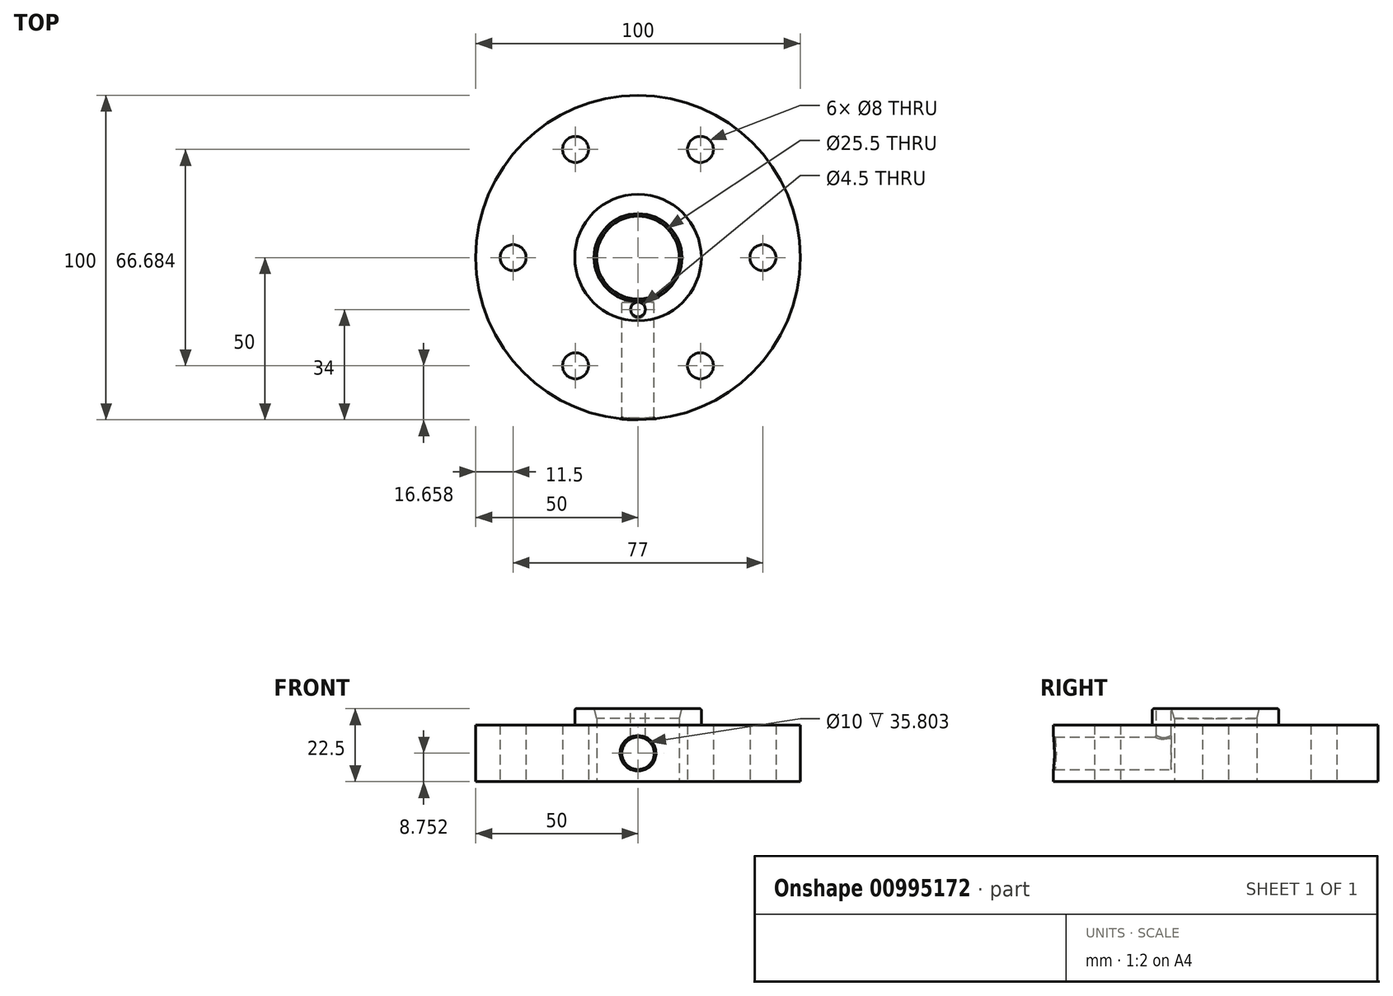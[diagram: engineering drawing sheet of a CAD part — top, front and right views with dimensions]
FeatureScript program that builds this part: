
annotation { "Feature Type Name" : "Feature", "Feature Type Description" : "" }
export const myFeature = defineFeature(function(context is Context, id is Id, definition is map)
    precondition{}
    {
        {
            var Q0;
            Q0=qCreatedBy(makeId("Top.planeOp"),FACE);
            var sketch = newSketch(context, id + "F0", { "sketchPlane" : qUnion([Q0])});
            skCircle(sketch, "E0", {"center": v(0, 0) * mm, "radius": 50 * mm});
            skCircle(sketch, "E1", {"center": v(0, 0) * mm, "radius": 19.5 * mm});
            skCircle(sketch, "E2", {"center": v(0, 0) * mm, "radius": 12.75 * mm});
            skCircle(sketch, "E3", {"center": v(-38.5, 0) * mm, "radius": 4 * mm});
            skCircle(sketch, "E4.1.0", {"center": v(-19.25, -33.34) * mm, "radius": 4 * mm});
            skCircle(sketch, "E4.2.0", {"center": v(19.25, -33.34) * mm, "radius": 4 * mm});
            skCircle(sketch, "E4.3.0", {"center": v(38.5, 0) * mm, "radius": 4 * mm});
            skCircle(sketch, "E4.4.0", {"center": v(19.25, 33.34) * mm, "radius": 4 * mm});
            skCircle(sketch, "E4.5.0", {"center": v(-19.25, 33.34) * mm, "radius": 4 * mm});
            skSolve(sketch);
        }
        {
            var Q0;
            Q0=makeQuery(id+"F0.imprint","IMPRINT",FACE,{"disambiguationData":[TD([[makeQuery(id+"F0.imprint","IMPRINT",EDGE,{"derivedFrom":sQuery(id+"F0.wireOp",EDGE,"E0")}),1.0]])]});
            extrude(context, id + "F1", {"entities" : qUnion([Q0]), "depth" : 17.5 * mm, "offsetDistance" : 25 * mm});
        }
        {
            var Q0;
            Q0=makeQuery(id+"F0.imprint","IMPRINT",FACE,{"disambiguationData":[TD([[makeQuery(id+"F0.imprint","IMPRINT",EDGE,{"derivedFrom":sQuery(id+"F0.wireOp",EDGE,"E1")}),1.0]])]});
            extrude(context, id + "F2", {"entities" : qUnion([Q0]), "operationType" : NewBodyOperationType.ADD, "depth" : 22.5 * mm, "offsetDistance" : 25 * mm});
        }
        {
            var Q0;
            Q0=qCreatedBy(makeId("Front.planeOp"),FACE);
            cPlane(context, id + "F3", {"entities" : qUnion([Q0]), "cplaneType" : CPlaneType.OFFSET, "offset" : 13.7 * mm, "width" : 150 * mm, "height" : 150 * mm});
        }
        {
            var Q0;
            Q0=qCreatedBy(id+"F3.planeOp",FACE);
            var sketch = newSketch(context, id + "F4", { "sketchPlane" : qUnion([Q0])});
            skCircle(sketch, "E5", {"center": v(0, 8.75) * mm, "radius": 5 * mm});
            skSolve(sketch);
        }
        {
            var Q0;
            Q0 = qSketchRegion(id + "F4", true);
            extrude(context, id + "F5", {"entities" : qUnion([Q0]), "operationType" : NewBodyOperationType.REMOVE, "depth" : 52 * mm, "offsetDistance" : 25 * mm});
        }
        {
            var Q0;
            Q0=makeQuery(id+"F2.opExtrude","CAP_FACE",FACE,{"disambiguationData":[OSD([sQuery(id+"F0.wireOp",EDGE,"E1"),sQuery(id+"F0.wireOp",EDGE,"E2")])],"isStart":false});
            var sketch = newSketch(context, id + "F6", { "sketchPlane" : qUnion([Q0])});
            skCircle(sketch, "E6", {"center": v(0, -16) * mm, "radius": 2.25 * mm});
            skSolve(sketch);
        }
        {
            var Q0;
            Q0=makeQuery(id+"F6.imprint","IMPRINT",FACE,{"disambiguationData":[TD([[makeQuery(id+"F6.imprint","IMPRINT",EDGE,{"derivedFrom":sQuery(id+"F6.wireOp",EDGE,"E6")}),1.0]])]});
            extrude(context, id + "F7", {"entities" : qUnion([Q0]), "operationType" : NewBodyOperationType.REMOVE, "oppositeDirection" : true, "depth" : 10 * mm, "offsetDistance" : 25 * mm});
        }
        {
            var Q0;
            Q0=makeQuery(id+"F2.opExtrude","CAP_EDGE",EDGE,{"disambiguationData":[OSD([sQuery(id+"F0.wireOp",EDGE,"E2")])],"isStart":false});
            chamfer(context, id + "F8", {"entities" : qUnion([Q0]), "chamferType" : ChamferType.OFFSET_ANGLE, "width" : 3 * mm, "oppositeDirection" : false, "angle" : 15 * degree, "tangentPropagation" : true});
        }
        {
            var Q0;
            Q0=makeQuery(id+"F2.opExtrude","CAP_EDGE",EDGE,{"disambiguationData":[OSD([sQuery(id+"F0.wireOp",EDGE,"E1")])],"isStart":false});
            var Q1;
            Q1=makeQuery(id+"F7.boolean.opBoolean","COPY",EDGE,{"derivedFrom":makeQuery(id+"F7.opExtrude","CAP_EDGE",EDGE,{"disambiguationData":[OSD([sQuery(id+"F6.wireOp",EDGE,"E6")])],"isStart":true})});
            var Q2;
            Q2=makeQuery(id+"F5.boolean.opBoolean","INTERSECT",EDGE,{"derivedFrom":[makeQuery(id+"F1.opExtrude","SWEPT_FACE",FACE,{"disambiguationData":[OSD([sQuery(id+"F0.wireOp",EDGE,"E0")])]}),makeQuery(id+"F5.opExtrude","SWEPT_FACE",FACE,{"disambiguationData":[OSD([sQuery(id+"F4.wireOp",EDGE,"E5")])]})]});
            fillet(context, id + "F9", {"entities" : qUnion([Q0, Q1, Q2]), "radius" : .5 * mm, "tangentPropagation" : true, "allowEdgeOverflow" : false});
        }
        {
            var Q0;
            Q0=makeQuery(id+"F7.boolean.opBoolean","INTERSECT",EDGE,{"derivedFrom":[makeQuery(id+"F5.boolean.opBoolean","COPY",FACE,{"derivedFrom":makeQuery(id+"F5.opExtrude","SWEPT_FACE",FACE,{"disambiguationData":[OSD([sQuery(id+"F4.wireOp",EDGE,"E5")])]})}),makeQuery(id+"F7.opExtrude","SWEPT_FACE",FACE,{"disambiguationData":[OSD([sQuery(id+"F6.wireOp",EDGE,"E6")])]})]});
            chamfer(context, id + "F10", {"entities" : qUnion([Q0]), "width" : .5 * mm, "tangentPropagation" : true});
        }
    });
